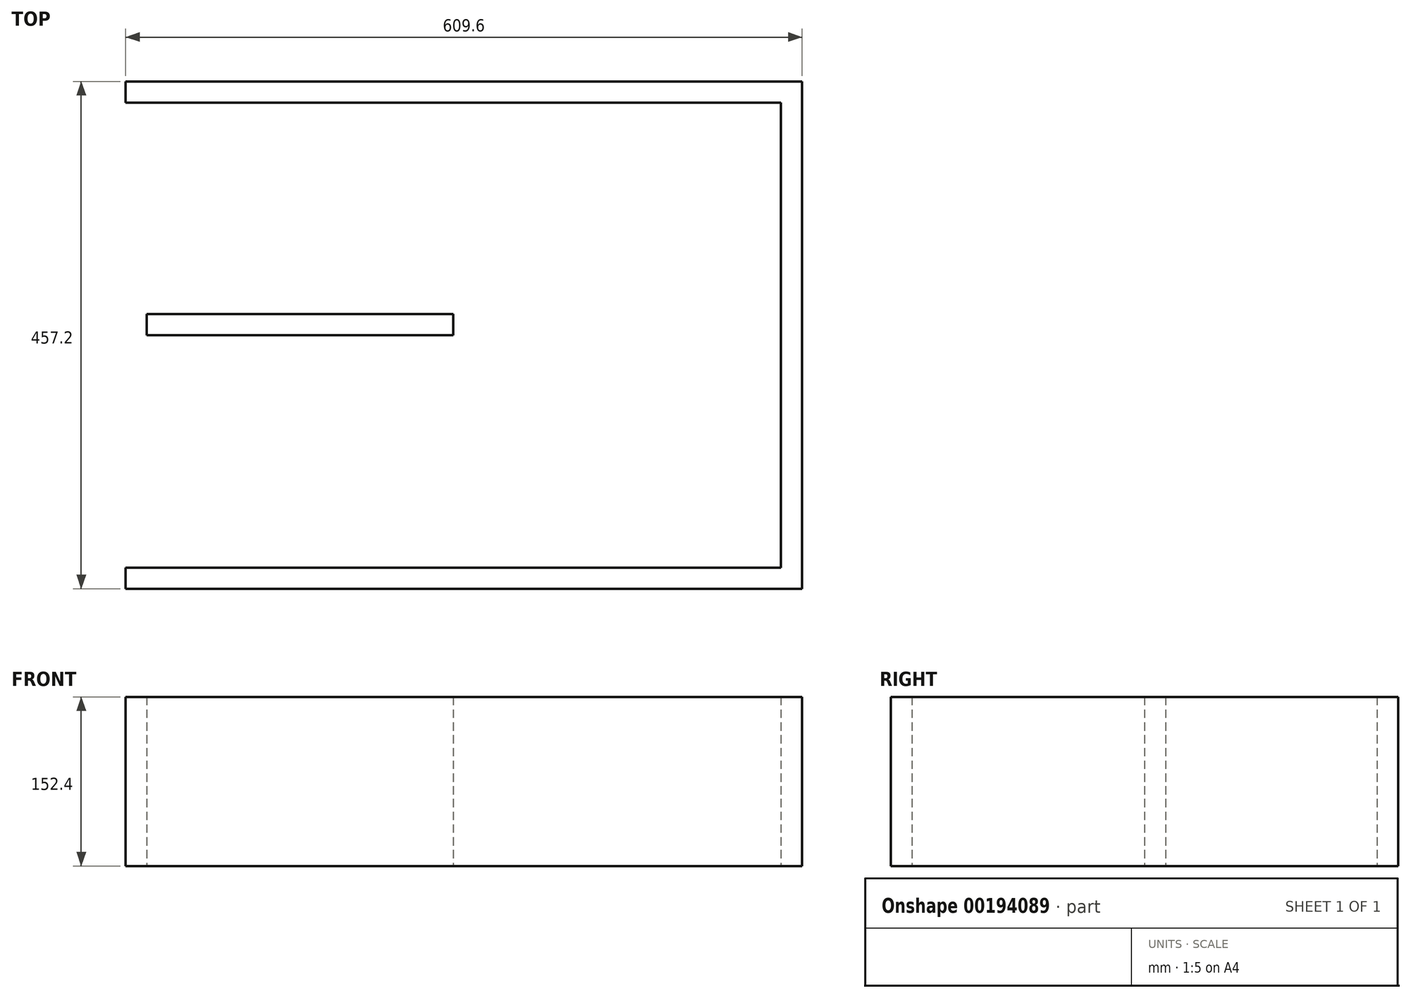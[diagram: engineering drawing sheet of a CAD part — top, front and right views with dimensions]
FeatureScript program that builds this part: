
annotation { "Feature Type Name" : "Feature", "Feature Type Description" : "" }
export const myFeature = defineFeature(function(context is Context, id is Id, definition is map)
    precondition{}
    {
        {
            var Q0;
            Q0=qCreatedBy(makeId("Top.planeOp"),FACE);
            var sketch = newSketch(context, id + "F0", { "sketchPlane" : qUnion([Q0])});
            skLineSegment(sketch, "E0.bottom", {"start": v(-492.25, 387.55) * mm, "end": v(117.35, 387.55) * mm});
            skLineSegment(sketch, "E0.top", {"start": v(-492.25, -69.65) * mm, "end": v(117.35, -69.65) * mm});
            skLineSegment(sketch, "E0.left", {"start": v(-492.25, 387.55) * mm, "end": v(-492.25, -69.65) * mm});
            skLineSegment(sketch, "E0.right", {"start": v(117.35, 387.55) * mm, "end": v(117.35, -69.65) * mm});
            skLineSegment(sketch, "E1", {"start": v(-492.25, -50.6) * mm, "end": v(117.35, -50.6) * mm});
            skLineSegment(sketch, "E2", {"start": v(-492.25, 368.5) * mm, "end": v(117.35, 368.5) * mm});
            skLineSegment(sketch, "E3", {"start": v(-473.2, 368.5) * mm, "end": v(-473.2, -50.6) * mm});
            skLineSegment(sketch, "E4", {"start": v(98.3, 368.5) * mm, "end": v(98.3, -50.6) * mm});
            skLineSegment(sketch, "E5.bottom", {"start": v(-196.98, 368.5) * mm, "end": v(-177.93, 368.5) * mm});
            skLineSegment(sketch, "E5.top", {"start": v(-196.98, -50.6) * mm, "end": v(-177.93, -50.6) * mm});
            skLineSegment(sketch, "E5.left", {"start": v(-196.98, 368.5) * mm, "end": v(-196.98, -50.6) * mm});
            skLineSegment(sketch, "E5.right", {"start": v(-177.93, 368.5) * mm, "end": v(-177.93, -50.6) * mm});
            skLineSegment(sketch, "E6.bottom", {"start": v(-473.2, 178) * mm, "end": v(-196.98, 178) * mm});
            skLineSegment(sketch, "E6.top", {"start": v(-473.2, 158.95) * mm, "end": v(-196.98, 158.95) * mm});
            skLineSegment(sketch, "E6.left", {"start": v(-473.2, 178) * mm, "end": v(-473.2, 158.95) * mm});
            skLineSegment(sketch, "E6.right", {"start": v(-196.98, 178) * mm, "end": v(-196.98, 158.95) * mm});
            skSolve(sketch);
        }
        {
            var Q0;
            {var subQ5=sQuery(id+"F0.wireOp",EDGE,"E6.left");Q0=makeQuery(id+"F0.imprint","IMPRINT",FACE,{"disambiguationData":[TD([[makeQuery(id+"F0.imprint","IMPRINT",EDGE,{"derivedFrom":subQ5}),-1.0]])]});}
            var Q1;
            Q1=makeQuery(id+"F0.imprint","IMPRINT",FACE,{"disambiguationData":[TD([[makeQuery(id+"F0.imprint","IMPRINT",EDGE,{"derivedFrom":sQuery(id+"F0.wireOp",EDGE,"E6.bottom")}),-1.0]])]});
            var Q2;
            {var subQ5=sQuery(id+"F0.wireOp",EDGE,"E0.bottom");Q2=makeQuery(id+"F0.imprint","IMPRINT",FACE,{"disambiguationData":[TD([[makeQuery(id+"F0.imprint","IMPRINT",EDGE,{"derivedFrom":subQ5}),-1.0]])]});}
            var Q3;
            {var subQ3=sQuery(id+"F0.wireOp",EDGE,"E5.bottom");Q3=makeQuery(id+"F0.imprint","IMPRINT",FACE,{"disambiguationData":[TD([[makeQuery(id+"F0.imprint","IMPRINT",EDGE,{"derivedFrom":subQ3}),-1.0]])]});}
            var Q4;
            {var subQ5=sQuery(id+"F0.wireOp",EDGE,"E4");Q4=makeQuery(id+"F0.imprint","IMPRINT",FACE,{"disambiguationData":[TD([[makeQuery(id+"F0.imprint","IMPRINT",EDGE,{"derivedFrom":subQ5}),1.0]])]});}
            var Q5;
            {var subQ4=sQuery(id+"F0.wireOp",EDGE,"E0.top");Q5=makeQuery(id+"F0.imprint","IMPRINT",FACE,{"disambiguationData":[TD([[makeQuery(id+"F0.imprint","IMPRINT",EDGE,{"derivedFrom":subQ4}),1.0]])]});}
            extrude(context, id + "F1", {"entities" : qUnion([Q0, Q1, Q2, Q3, Q4, Q5]), "depth" : 152.4 * mm});
        }
    });
